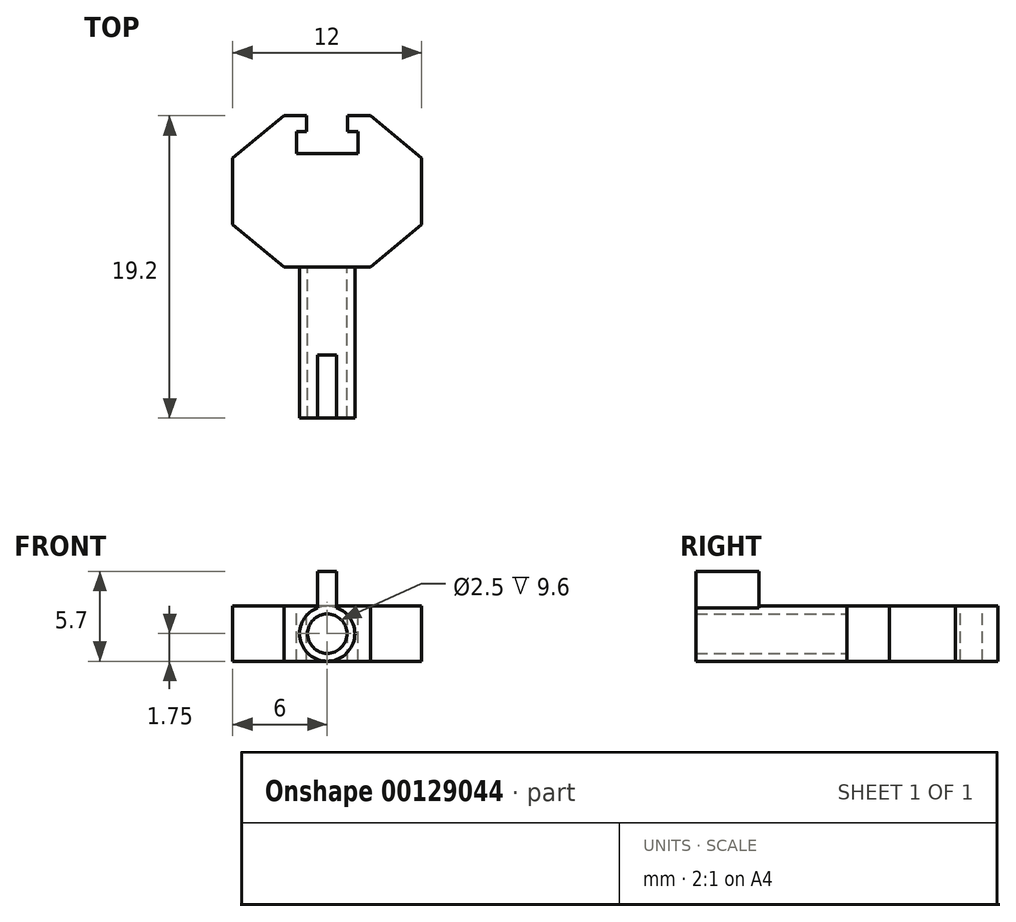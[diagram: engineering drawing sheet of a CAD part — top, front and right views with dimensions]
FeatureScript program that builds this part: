
annotation { "Feature Type Name" : "Feature", "Feature Type Description" : "" }
export const myFeature = defineFeature(function(context is Context, id is Id, definition is map)
    precondition{}
    {
        {
            var Q0;
            Q0=qCreatedBy(makeId("Top.planeOp"),FACE);
            var sketch = newSketch(context, id + "F0", { "sketchPlane" : qUnion([Q0])});
            skLineSegment(sketch, "E0", {"start": v(-5.5, 2.7) * mm, "end": v(0, 2.7) * mm});
            skLineSegment(sketch, "E1", {"start": v(0, 2.7) * mm, "end": v(3.25, 0) * mm});
            skLineSegment(sketch, "E2", {"start": v(3.25, 0) * mm, "end": v(3.25, -4.2) * mm});
            skLineSegment(sketch, "E3", {"start": v(3.25, -4.2) * mm, "end": v(0, -6.9) * mm});
            skLineSegment(sketch, "E4", {"start": v(0, -6.9) * mm, "end": v(-5.5, -6.9) * mm});
            skLineSegment(sketch, "E5", {"start": v(-5.5, -6.9) * mm, "end": v(-8.75, -4.2) * mm});
            skLineSegment(sketch, "E6", {"start": v(-8.75, -4.2) * mm, "end": v(-8.75, 0) * mm});
            skLineSegment(sketch, "E7", {"start": v(-8.75, 0) * mm, "end": v(-5.5, 2.7) * mm});
            skSolve(sketch);
        }
        {
            var Q0;
            Q0=makeQuery(id+"F0.imprint","IMPRINT",FACE,{"disambiguationData":[TD([[makeQuery(id+"F0.imprint","IMPRINT",EDGE,{"derivedFrom":sQuery(id+"F0.wireOp",EDGE,"E0")}),-1.0]])]});
            extrude(context, id + "F1", {"entities" : qUnion([Q0]), "depth" : 3.5 * mm});
        }
        {
            var Q0;
            Q0=makeQuery(id+"F1.opExtrude","SWEPT_FACE",FACE,{"disambiguationData":[OSD([sQuery(id+"F0.wireOp",EDGE,"E4")])]});
            var sketch = newSketch(context, id + "F2", { "sketchPlane" : qUnion([Q0])});
            skCircle(sketch, "E8", {"center": v(-2.75, 1.75) * mm, "radius": 1.75 * mm});
            skPoint(sketch, "E9", {"position": v(-2.75, 0) * mm});
            skCircle(sketch, "E10", {"center": v(-2.75, 1.75) * mm, "radius": 1.25 * mm});
            skSolve(sketch);
        }
        {
            var Q0;
            Q0 = qSketchRegion(id + "F2", true);
            extrude(context, id + "F3", {"entities" : qUnion([Q0]), "operationType" : NewBodyOperationType.ADD, "depth" : 9.6 * mm});
        }
        {
            var Q0;
            Q0=makeQuery(id+"F1.opExtrude","CAP_FACE",FACE,{"disambiguationData":[OSD([sQuery(id+"F0.wireOp",EDGE,"E0"),sQuery(id+"F0.wireOp",EDGE,"E1"),sQuery(id+"F0.wireOp",EDGE,"E2"),sQuery(id+"F0.wireOp",EDGE,"E3"),sQuery(id+"F0.wireOp",EDGE,"E4"),sQuery(id+"F0.wireOp",EDGE,"E5"),sQuery(id+"F0.wireOp",EDGE,"E6"),sQuery(id+"F0.wireOp",EDGE,"E7")])],"isStart":false});
            var sketch = newSketch(context, id + "F4", { "sketchPlane" : qUnion([Q0])});
            skLineSegment(sketch, "E11", {"start": v(-4.05, 2.7) * mm, "end": v(-4.05, 1.7) * mm});
            skLineSegment(sketch, "E12", {"start": v(-4.05, 1.7) * mm, "end": v(-4.7, 1.7) * mm});
            skLineSegment(sketch, "E13", {"start": v(-4.7, 1.7) * mm, "end": v(-4.7, 0.3) * mm});
            skLineSegment(sketch, "E14", {"start": v(-4.7, 0.3) * mm, "end": v(-0.8, 0.3) * mm});
            skLineSegment(sketch, "E15", {"start": v(-0.8, 0.3) * mm, "end": v(-0.8, 1.7) * mm});
            skLineSegment(sketch, "E16", {"start": v(-0.8, 1.7) * mm, "end": v(-1.45, 1.7) * mm});
            skLineSegment(sketch, "E17", {"start": v(-1.45, 1.7) * mm, "end": v(-1.45, 2.7) * mm});
            skLineSegment(sketch, "E18", {"start": v(-1.45, 2.7) * mm, "end": v(-4.05, 2.7) * mm});
            skPoint(sketch, "E19", {"position": v(-2.75, 2.7) * mm});
            skSolve(sketch);
        }
        {
            var Q0;
            Q0=makeQuery(id+"F4.imprint","IMPRINT",FACE,{"disambiguationData":[TD([[makeQuery(id+"F4.imprint","IMPRINT",EDGE,{"derivedFrom":sQuery(id+"F4.wireOp",EDGE,"E11")}),1.0]])]});
            extrude(context, id + "F5", {"entities" : qUnion([Q0]), "operationType" : NewBodyOperationType.REMOVE, "endBound" : BoundingType.THROUGH_ALL, "oppositeDirection" : true, "depth" : 25.4 * mm});
        }
        {
            var Q0;
            Q0=makeQuery(id+"F1.opExtrude","CAP_FACE",FACE,{"disambiguationData":[OSD([sQuery(id+"F0.wireOp",EDGE,"E0"),sQuery(id+"F0.wireOp",EDGE,"E1"),sQuery(id+"F0.wireOp",EDGE,"E2"),sQuery(id+"F0.wireOp",EDGE,"E3"),sQuery(id+"F0.wireOp",EDGE,"E4"),sQuery(id+"F0.wireOp",EDGE,"E5"),sQuery(id+"F0.wireOp",EDGE,"E6"),sQuery(id+"F0.wireOp",EDGE,"E7")])],"isStart":false});
            var sketch = newSketch(context, id + "F6", { "sketchPlane" : qUnion([Q0])});
            skLineSegment(sketch, "E20.bottom", {"start": v(-3.35, -12.5) * mm, "end": v(-2.15, -12.5) * mm});
            skLineSegment(sketch, "E20.top", {"start": v(-3.35, -16.5) * mm, "end": v(-2.15, -16.5) * mm});
            skLineSegment(sketch, "E20.left", {"start": v(-3.35, -12.5) * mm, "end": v(-3.35, -16.5) * mm});
            skLineSegment(sketch, "E20.right", {"start": v(-2.15, -12.5) * mm, "end": v(-2.15, -16.5) * mm});
            skPoint(sketch, "E21", {"position": v(-2.75, -16.5) * mm});
            skSolve(sketch);
        }
        {
            var Q0;
            Q0=makeQuery(id+"F6.imprint","IMPRINT",FACE,{"disambiguationData":[TD([[makeQuery(id+"F6.imprint","IMPRINT",EDGE,{"derivedFrom":sQuery(id+"F6.wireOp",EDGE,"E20.bottom")}),-1.0]])]});
            extrude(context, id + "F7", {"entities" : qUnion([Q0]), "operationType" : NewBodyOperationType.ADD, "depth" : 2.2 * mm, "hasSecondDirection" : true, "secondDirectionBound" : SecondDirectionBoundingType.UP_TO_NEXT, "secondDirectionOppositeDirection" : true, "secondDirectionDepth" : 25.4 * mm});
        }
    });
